FCSTD DOCUMENT  (FreeCAD 0.16R6712 (Git))
Label: BordePCB
License: All rights reserved
LicenseURL: http://es.wikipedia.org/wiki/Todos_los_derechos_reservados
objects: Sketcher::SketchObject×1
note: 1 computed .brp shape members not serialized (recipe doc carries the construction recipe); baked Part::Feature solids carry a one-line shape summary decoded from their .brp

FEATURE [Sketcher::SketchObject] Sketch  label="Borde"
  sketch-geometry (35):
    g0: LineSegment StartX=-28.2634 StartY=19.6801 StartZ=0 EndX=30.2366 EndY=19.6801 EndZ=0
    g1: LineSegment StartX=33.1739 StartY=10.5458 StartZ=0 EndX=20.091 EndY=1.28627 EndZ=0
    g2: LineSegment StartX=16.0471 StartY=0 StartZ=0 EndX=-13.9529 EndY=0 EndZ=0
    g3: LineSegment StartX=-17.9898 StartY=1.28127 StartZ=0 EndX=-31.0841 EndY=10.5246 EndZ=0
    g4: ArcOfCircle CenterX=-13.9529 CenterY=7 CenterZ=0 NormalX=0 NormalY=0 NormalZ=1 Radius=7 StartAngle=4.09771 EndAngle=4.71239
    g5: ArcOfCircle CenterX=16.0471 CenterY=7 CenterZ=0 NormalX=0 NormalY=0 NormalZ=1 Radius=7 StartAngle=4.71239 EndAngle=5.3283
    g6: Circle [constr] CenterX=-25.2634 CenterY=14.6801 CenterZ=0 NormalX=0 NormalY=0 NormalZ=1 Radius=2.5
    g7: Circle [constr] CenterX=-17.7634 CenterY=14.6801 CenterZ=0 NormalX=0 NormalY=0 NormalZ=1 Radius=2.5
    g8: Circle [constr] CenterX=-10.2634 CenterY=14.6801 CenterZ=0 NormalX=0 NormalY=0 NormalZ=1 Radius=2.5
    g9: Circle [constr] CenterX=-2.76338 CenterY=14.6801 CenterZ=0 NormalX=0 NormalY=0 NormalZ=1 Radius=2.5
    g10: Circle [constr] CenterX=4.73662 CenterY=14.6801 CenterZ=0 NormalX=0 NormalY=0 NormalZ=1 Radius=2.5
    g11: Circle [constr] CenterX=12.2366 CenterY=14.6801 CenterZ=0 NormalX=0 NormalY=0 NormalZ=1 Radius=2.5
    g12: Circle [constr] CenterX=19.7366 CenterY=14.6801 CenterZ=0 NormalX=0 NormalY=0 NormalZ=1 Radius=2.5
    g13: Circle [constr] CenterX=27.2366 CenterY=14.6801 CenterZ=0 NormalX=0 NormalY=0 NormalZ=1 Radius=2.5
    g14: LineSegment [constr] StartX=-25.2634 StartY=14.6801 StartZ=0 EndX=27.2366 EndY=14.6801 EndZ=0
    g15: LineSegment [constr] StartX=-11.9529 StartY=5 StartZ=0 EndX=14.0471 EndY=5 EndZ=0
    g16: LineSegment [constr] StartX=14.0471 StartY=5 StartZ=0 EndX=14.0471 EndY=3 EndZ=0
    g17: LineSegment [constr] StartX=14.0471 StartY=3 StartZ=0 EndX=-11.9529 EndY=3 EndZ=0
    g18: LineSegment [constr] StartX=-11.9529 StartY=3 StartZ=0 EndX=-11.9529 EndY=5 EndZ=0
    g19: LineSegment [constr] StartX=-16.0841 StartY=10.2747 StartZ=0 EndX=-3.08412 EndY=10.2747 EndZ=0
    g20: LineSegment [constr] StartX=-3.08412 StartY=10.2747 StartZ=0 EndX=-3.08412 EndY=8.27473 EndZ=0
    g21: LineSegment [constr] StartX=-3.08412 StartY=8.27473 StartZ=0 EndX=-16.0841 EndY=8.27473 EndZ=0
    g22: LineSegment [constr] StartX=-16.0841 StartY=8.27473 StartZ=0 EndX=-16.0841 EndY=10.2747 EndZ=0
    g23: LineSegment [constr] StartX=5.17388 StartY=10.2747 StartZ=0 EndX=18.1739 EndY=10.2747 EndZ=0
    g24: LineSegment [constr] StartX=18.1739 StartY=10.2747 StartZ=0 EndX=18.1739 EndY=8.27473 EndZ=0
    g25: LineSegment [constr] StartX=18.1739 StartY=8.27473 StartZ=0 EndX=5.17388 EndY=8.27473 EndZ=0
    g26: LineSegment [constr] StartX=5.17388 StartY=8.27473 StartZ=0 EndX=5.17388 EndY=10.2747 EndZ=0
    g27: LineSegment StartX=-33.2333 StartY=16.5288 StartZ=0 EndX=-33.2333 EndY=13.0288 EndZ=0
    g28: LineSegment StartX=-31.0841 StartY=10.5246 StartZ=0 EndX=-33.2333 EndY=13.0288 EndZ=0
    g29: LineSegment StartX=-28.2634 StartY=19.6801 StartZ=0 EndX=-30.8184 EndY=19.1987 EndZ=0
    g30: LineSegment StartX=-33.2333 StartY=16.5288 StartZ=0 EndX=-30.8184 EndY=19.1987 EndZ=0
    g31: LineSegment StartX=30.2366 StartY=19.6801 StartZ=0 EndX=32.7877 EndY=19.1783 EndZ=0
    g32: LineSegment StartX=33.1739 StartY=10.5458 StartZ=0 EndX=35.2832 EndY=13.0836 EndZ=0
    g33: LineSegment StartX=35.2832 StartY=16.5836 StartZ=0 EndX=35.2832 EndY=13.0836 EndZ=0
    g34: LineSegment StartX=32.7877 StartY=19.1783 StartZ=0 EndX=35.2832 EndY=16.5836 EndZ=0
  constraints (92):
    c: Horizontal(g0)
    c: Horizontal(g2)
    c: Tangent(g3,g4) = 1.5708
    c: Tangent(g2,g4) = 1.5708
    c: Tangent(g2,g5) = 1.5708
    c: Tangent(g1,g5) = 1.5708
    c: Equal(g4,g5)
    c: Radius(g6) = 2.5
    c: Equal(g6,g7)
    c: Equal(g7,g8)
    c: Equal(g8,g9)
    c: Equal(g9,g10)
    c: Equal(g10,g11)
    c: Equal(g11,g12)
    c: Equal(g12,g13)
    c: DistanceX(g6,g7) = 7.5
    c: DistanceX(g7,g8) = 7.5
    c: DistanceX(g8,g9) = 7.5
    c: DistanceX(g9,g10) = 7.5
    c: DistanceX(g10,g11) = 7.5
    c: DistanceX(g11,g12) = 7.5
    c: DistanceX(g12,g13) = 7.5
    c: PointOnObject(g-1,g2)
    c: DistanceY(g6,g0) = 5
    c: Coincident(g14,g6)
    c: Coincident(g14,g13)
    c: Horizontal(g14)
    c: PointOnObject(g7,g14)
    c: PointOnObject(g8,g14)
    c: PointOnObject(g9,g14)
    c: PointOnObject(g10,g14)
    c: PointOnObject(g11,g14)
    c: PointOnObject(g12,g14)
    c: DistanceX(g0,g6) = 3
    c: DistanceX(g13,g0) = 3
    c: Coincident(g15,g16)
    c: Coincident(g16,g17)
    c: Coincident(g17,g18)
    c: Coincident(g18,g15)
    c: Horizontal(g15)
    c: Horizontal(g17)
    c: Vertical(g16)
    c: Vertical(g18)
    c: DistanceX(g15,g15) = 26
    c: DistanceY(g16,g16) = 2
    c: DistanceX(g2,g2) = 30
    c: DistanceX(g2,g17) = 2
    c: DistanceY(g2,g17) = 3
    c: Radius(g4) = 7
    c: Equal(g3,g1)
    c: Coincident(g19,g20)
    c: Coincident(g20,g21)
    c: Coincident(g21,g22)
    c: Coincident(g22,g19)
    c: Horizontal(g19)
    c: Horizontal(g21)
    c: Vertical(g20)
    c: Vertical(g22)
    c: Coincident(g23,g24)
    c: Coincident(g24,g25)
    c: Coincident(g25,g26)
    c: Coincident(g26,g23)
    c: Horizontal(g23)
    c: Horizontal(g25)
    c: Vertical(g24)
    c: Vertical(g26)
    c: Equal(g19,g23)
    c: DistanceX(g19,g19) = 13
    c: Equal(g26,g20)
    c: DistanceY(g24,g24) = 2
    c: DistanceX(g23,g1) = 15
    c: DistanceX(g3,g19) = 15
    c: Vertical(g27)
    c: Coincident(g28,g3)
    c: Coincident(g29,g0)
    c: Coincident(g31,g0)
    c: Coincident(g32,g1)
    c: Vertical(g33)
    c: Coincident(g31,g34)
    c: Coincident(g34,g33)
    c: Coincident(g33,g32)
    c: Coincident(g27,g28)
    c: Coincident(g27,g30)
    c: Coincident(g29,g30)
    c: Distance(g31) = 2.6
    c: Equal(g29,g31)
    c: Distance(g34) = 3.6
    c: Equal(g30,g34)
    c: DistanceY(g27,g27) = 3.5
    c: Equal(g27,g33)
    c: Distance(g32) = 3.3
    c: Equal(g28,g32)
